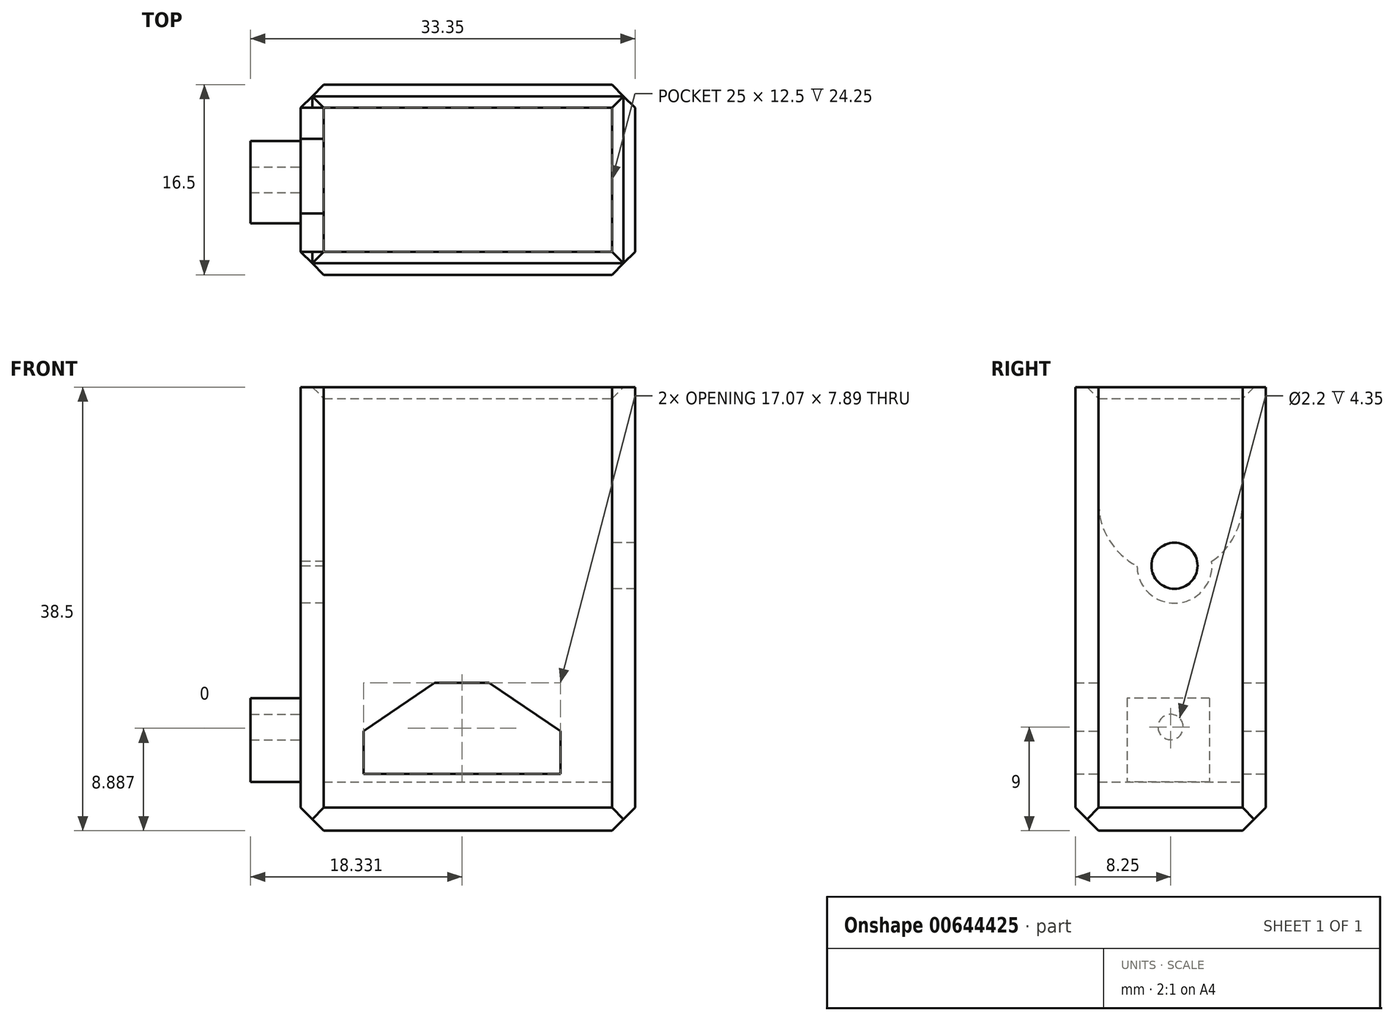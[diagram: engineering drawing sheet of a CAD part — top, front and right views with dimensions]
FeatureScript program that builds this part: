
annotation { "Feature Type Name" : "Feature", "Feature Type Description" : "" }
export const myFeature = defineFeature(function(context is Context, id is Id, definition is map)
    precondition{}
    {
        {
            var Q0;
            Q0=qCreatedBy(makeId("Top.planeOp"),FACE);
            var sketch = newSketch(context, id + "F0", { "sketchPlane" : qUnion([Q0])});
            skLineSegment(sketch, "E0.bottom", {"start": v(0, 0) * mm, "end": v(29, 0) * mm});
            skLineSegment(sketch, "E0.top", {"start": v(0, 16.5) * mm, "end": v(29, 16.5) * mm});
            skLineSegment(sketch, "E0.left", {"start": v(0, 0) * mm, "end": v(0, 16.5) * mm});
            skLineSegment(sketch, "E0.right", {"start": v(29, 0) * mm, "end": v(29, 16.5) * mm});
            skSolve(sketch);
        }
        {
            var Q0;
            Q0=makeQuery(id+"F0.imprint","IMPRINT",FACE,{"disambiguationData":[TD([[makeQuery(id+"F0.imprint","IMPRINT",EDGE,{"derivedFrom":sQuery(id+"F0.wireOp",EDGE,"E0.bottom")}),1.0]])]});
            extrude(context, id + "F1", {"entities" : qUnion([Q0]), "depth" : 38.5 * mm, "offsetDistance" : 25 * mm});
        }
        {
            var Q0;
            Q0=makeQuery(id+"F1.opExtrude","CAP_FACE",FACE,{"disambiguationData":[OSD([sQuery(id+"F0.wireOp",EDGE,"E0.bottom"),sQuery(id+"F0.wireOp",EDGE,"E0.top"),sQuery(id+"F0.wireOp",EDGE,"E0.left"),sQuery(id+"F0.wireOp",EDGE,"E0.right")])],"isStart":false});
            shell(context, id + "F2", {"entities" : qUnion([Q0]), "thickness" : 2 * mm});
        }
        {
            var Q0;
            Q0=makeQuery(id+"F2.opShell","OFFSET_FACE",FACE,{"disambiguationData":[OSD([sQuery(id+"F0.wireOp",EDGE,"E0.bottom"),sQuery(id+"F0.wireOp",EDGE,"E0.top"),sQuery(id+"F0.wireOp",EDGE,"E0.left"),sQuery(id+"F0.wireOp",EDGE,"E0.right")])]});
            extrude(context, id + "F3", {"entities" : qUnion([Q0]), "operationType" : NewBodyOperationType.ADD, "depth" : 2.25 * mm, "offsetDistance" : 25 * mm});
        }
        {
            var Q0;
            Q0=makeQuery(id+"F1.opExtrude","SWEPT_EDGE",EDGE,{"disambiguationData":[OSD([sQuery(id+"F0.wireOp",EDGE,"E0.bottom"),sQuery(id+"F0.wireOp",EDGE,"E0.left")])]});
            chamfer(context, id + "F4", {"entities" : qUnion([Q0]), "width" : 2 * mm, "tangentPropagation" : true});
        }
        {
            var Q0;
            Q0=makeQuery(id+"F1.opExtrude","SWEPT_EDGE",EDGE,{"disambiguationData":[OSD([sQuery(id+"F0.wireOp",EDGE,"E0.top"),sQuery(id+"F0.wireOp",EDGE,"E0.left")])]});
            var Q1;
            Q1=makeQuery(id+"F1.opExtrude","SWEPT_EDGE",EDGE,{"disambiguationData":[OSD([sQuery(id+"F0.wireOp",EDGE,"E0.bottom"),sQuery(id+"F0.wireOp",EDGE,"E0.right")])]});
            chamfer(context, id + "F5", {"entities" : qUnion([Q0, Q1]), "width" : 2 * mm, "tangentPropagation" : true});
        }
        {
            var Q0;
            Q0=makeQuery(id+"F1.opExtrude","SWEPT_EDGE",EDGE,{"disambiguationData":[OSD([sQuery(id+"F0.wireOp",EDGE,"E0.top"),sQuery(id+"F0.wireOp",EDGE,"E0.right")])]});
            chamfer(context, id + "F6", {"entities" : qUnion([Q0]), "width" : 2 * mm, "tangentPropagation" : true});
        }
        {
            var Q0;
            Q0=makeQuery(id+"F1.opExtrude","CAP_EDGE",EDGE,{"disambiguationData":[OSD([sQuery(id+"F0.wireOp",EDGE,"E0.bottom")])],"isStart":true});
            chamfer(context, id + "F7", {"entities" : qUnion([Q0]), "width" : 2 * mm, "tangentPropagation" : true});
        }
        {
            var Q0;
            Q0=makeQuery(id+"F1.opExtrude","CAP_EDGE",EDGE,{"disambiguationData":[OSD([sQuery(id+"F0.wireOp",EDGE,"E0.top")])],"isStart":true});
            chamfer(context, id + "F8", {"entities" : qUnion([Q0]), "width" : 2 * mm, "tangentPropagation" : true});
        }
        {
            var Q0;
            {var subQ0=sQuery(id+"F0.wireOp",EDGE,"E0.top");Q0=makeQuery(id+"F2.opShell","OFFSET_EDGE",EDGE,{"disambiguationData":[OSD([subQ0]),TDD([makeQuery(id+"F1.opExtrude","CAP_EDGE",EDGE,{"disambiguationData":[OSD([subQ0])],"isStart":false})])]});}
            var Q1;
            {var subQ0=sQuery(id+"F0.wireOp",EDGE,"E0.left");Q1=makeQuery(id+"F2.opShell","OFFSET_EDGE",EDGE,{"disambiguationData":[OSD([subQ0]),TDD([makeQuery(id+"F1.opExtrude","CAP_EDGE",EDGE,{"disambiguationData":[OSD([subQ0])],"isStart":false})])]});}
            var Q2;
            {var subQ0=sQuery(id+"F0.wireOp",EDGE,"E0.bottom");Q2=makeQuery(id+"F2.opShell","OFFSET_EDGE",EDGE,{"disambiguationData":[OSD([subQ0]),TDD([makeQuery(id+"F1.opExtrude","CAP_EDGE",EDGE,{"disambiguationData":[OSD([subQ0])],"isStart":false})])]});}
            var Q3;
            {var subQ0=sQuery(id+"F0.wireOp",EDGE,"E0.right");Q3=makeQuery(id+"F2.opShell","OFFSET_EDGE",EDGE,{"disambiguationData":[OSD([subQ0]),TDD([makeQuery(id+"F1.opExtrude","CAP_EDGE",EDGE,{"disambiguationData":[OSD([subQ0])],"isStart":false})])]});}
            chamfer(context, id + "F9", {"entities" : qUnion([Q0, Q1, Q2, Q3]), "width" : 1 * mm, "tangentPropagation" : true});
        }
        {
            var Q0;
            Q0=makeQuery(id+"F1.opExtrude","SWEPT_FACE",FACE,{"disambiguationData":[OSD([sQuery(id+"F0.wireOp",EDGE,"E0.top")])]});
            var sketch = newSketch(context, id + "F10", { "sketchPlane" : qUnion([Q0])});
            skLineSegment(sketch, "E1", {"start": v(-22.52, 8.66) * mm, "end": v(-22.52, 4.94) * mm});
            skLineSegment(sketch, "E2", {"start": v(-22.52, 4.94) * mm, "end": v(-5.44, 4.94) * mm});
            skLineSegment(sketch, "E3", {"start": v(-5.44, 4.94) * mm, "end": v(-5.44, 8.66) * mm});
            skLineSegment(sketch, "E4", {"start": v(-5.44, 8.66) * mm, "end": v(-11.62, 12.83) * mm});
            skLineSegment(sketch, "E5", {"start": v(-11.62, 12.83) * mm, "end": v(-16.34, 12.83) * mm});
            skLineSegment(sketch, "E6", {"start": v(-16.34, 12.83) * mm, "end": v(-22.52, 8.66) * mm});
            skSolve(sketch);
        }
        {
            var Q0;
            Q0=makeQuery(id+"F10.imprint","IMPRINT",FACE,{"disambiguationData":[TD([[makeQuery(id+"F10.imprint","IMPRINT",EDGE,{"derivedFrom":sQuery(id+"F10.wireOp",EDGE,"E1")}),1.0]])]});
            extrude(context, id + "F11", {"entities" : qUnion([Q0]), "operationType" : NewBodyOperationType.REMOVE, "endBound" : BoundingType.THROUGH_ALL, "oppositeDirection" : true, "depth" : 25 * mm, "offsetDistance" : 25 * mm});
        }
        {
            var Q0;
            Q0=makeQuery(id+"F1.opExtrude","CAP_EDGE",EDGE,{"disambiguationData":[OSD([sQuery(id+"F0.wireOp",EDGE,"E0.left")])],"isStart":true});
            chamfer(context, id + "F12", {"entities" : qUnion([Q0]), "width" : 2 * mm});
        }
        {
            var Q0;
            Q0=makeQuery(id+"F1.opExtrude","CAP_EDGE",EDGE,{"disambiguationData":[OSD([sQuery(id+"F0.wireOp",EDGE,"E0.right")])],"isStart":true});
            chamfer(context, id + "F13", {"entities" : qUnion([Q0]), "width" : 2 * mm});
        }
        {
            var Q0;
            Q0=makeQuery(id+"F1.opExtrude","SWEPT_FACE",FACE,{"disambiguationData":[OSD([sQuery(id+"F0.wireOp",EDGE,"E0.left")])]});
            var sketch = newSketch(context, id + "F14", { "sketchPlane" : qUnion([Q0])});
            skCircle(sketch, "E7", {"center": v(-8.25, 28.5) * mm, "radius": 6.25 * mm});
            skCircle(sketch, "E8", {"center": v(-8.59, 23) * mm, "radius": 3.25 * mm});
            skLineSegment(sketch, "E9.bottom", {"start": v(-2, 28.5) * mm, "end": v(-14.5, 28.5) * mm});
            skLineSegment(sketch, "E9.top", {"start": v(-2, 40.85) * mm, "end": v(-14.5, 40.85) * mm});
            skLineSegment(sketch, "E9.left", {"start": v(-2, 28.5) * mm, "end": v(-2, 40.85) * mm});
            skLineSegment(sketch, "E9.right", {"start": v(-14.5, 28.5) * mm, "end": v(-14.5, 40.85) * mm});
            skSolve(sketch);
        }
        {
            var Q0;
            {var subQ3=sQuery(id+"F0.wireOp",EDGE,"E0.left");var subQ8=makeQuery(id+"F1.opExtrude","CAP_EDGE",EDGE,{"disambiguationData":[OSD([subQ3])],"isStart":false});Q0=makeQuery(id+"F14.imprint","IMPRINT",FACE,{"disambiguationData":[TD([[makeQuery(id+"F14.imprint","IMPRINT",EDGE,{"derivedFrom":subQ8}),1.0]])]});}
            var Q1;
            {var subQ0=sQuery(id+"F14.wireOp",EDGE,"E9.top");Q1=makeQuery(id+"F14.imprint","IMPRINT",FACE,{"disambiguationData":[TD([[makeQuery(id+"F14.imprint","IMPRINT",EDGE,{"derivedFrom":subQ0}),1.0]])]});}
            var Q2;
            {var subQ0=sQuery(id+"F14.wireOp",EDGE,"E9.bottom");Q2=makeQuery(id+"F14.imprint","IMPRINT",FACE,{"disambiguationData":[TD([[makeQuery(id+"F14.imprint","IMPRINT",EDGE,{"derivedFrom":subQ0}),-1.0]])]});}
            var Q3;
            {var subQ0=sQuery(id+"F14.wireOp",EDGE,"E8");var subQ1=sQuery(id+"F14.wireOp",EDGE,"E7");var subQ2=makeQuery(id+"F14.imprint","INTERSECT",VERTEX,{"disambiguationData":[OD(0.0)],"derivedFrom":[subQ1,subQ0]});Q3=makeQuery(id+"F14.imprint","IMPRINT",FACE,{"disambiguationData":[TD([[makeQuery(id+"F14.imprint","IMPRINT",EDGE,{"disambiguationData":[TD([[subQ2,-1.0]])],"derivedFrom":subQ1}),1.0]])]});}
            var Q4;
            {var subQ0=sQuery(id+"F14.wireOp",EDGE,"E8");var subQ1=sQuery(id+"F14.wireOp",EDGE,"E7");var subQ2=makeQuery(id+"F14.imprint","INTERSECT",VERTEX,{"disambiguationData":[OD(0.0)],"derivedFrom":[subQ1,subQ0]});Q4=makeQuery(id+"F14.imprint","IMPRINT",FACE,{"disambiguationData":[TD([[makeQuery(id+"F14.imprint","IMPRINT",EDGE,{"disambiguationData":[TD([[subQ2,-1.0]])],"derivedFrom":subQ1}),-1.0]])]});}
            var Q5;
            {var subQ0=sQuery(id+"F14.wireOp",EDGE,"E9.bottom");Q5=makeQuery(id+"F14.imprint","IMPRINT",FACE,{"disambiguationData":[TD([[makeQuery(id+"F14.imprint","IMPRINT",EDGE,{"derivedFrom":subQ0}),1.0]])]});}
            extrude(context, id + "F15", {"entities" : qUnion([Q0, Q1, Q2, Q3, Q4, Q5]), "operationType" : NewBodyOperationType.REMOVE, "endBound" : BoundingType.UP_TO_NEXT, "oppositeDirection" : true, "depth" : 25 * mm, "offsetDistance" : 25 * mm});
        }
        {
            var Q0;
            Q0=makeQuery(id+"F2.opShell","OFFSET_FACE",FACE,{"disambiguationData":[OSD([sQuery(id+"F0.wireOp",EDGE,"E0.right")])]});
            var sketch = newSketch(context, id + "F16", { "sketchPlane" : qUnion([Q0])});
            skCircle(sketch, "E10", {"center": v(-8.59, 23) * mm, "radius": 2 * mm});
            skSolve(sketch);
        }
        {
            var Q0;
            Q0=makeQuery(id+"F16.imprint","IMPRINT",FACE,{"disambiguationData":[TD([[makeQuery(id+"F16.imprint","IMPRINT",EDGE,{"derivedFrom":sQuery(id+"F16.wireOp",EDGE,"E10")}),1.0]])]});
            extrude(context, id + "F17", {"entities" : qUnion([Q0]), "operationType" : NewBodyOperationType.REMOVE, "endBound" : BoundingType.THROUGH_ALL, "oppositeDirection" : true, "depth" : 25 * mm, "offsetDistance" : 25 * mm});
        }
        {
            var Q0;
            Q0=makeQuery(id+"F1.opExtrude","SWEPT_FACE",FACE,{"disambiguationData":[OSD([sQuery(id+"F0.wireOp",EDGE,"E0.left")])]});
            var sketch = newSketch(context, id + "F18", { "sketchPlane" : qUnion([Q0])});
            skLineSegment(sketch, "E11.bottom", {"start": v(-11.62, 11.5) * mm, "end": v(-4.48, 11.5) * mm});
            skLineSegment(sketch, "E11.top", {"start": v(-11.62, 4.25) * mm, "end": v(-4.48, 4.25) * mm});
            skLineSegment(sketch, "E11.left", {"start": v(-11.62, 11.5) * mm, "end": v(-11.62, 4.25) * mm});
            skLineSegment(sketch, "E11.right", {"start": v(-4.48, 11.5) * mm, "end": v(-4.48, 4.25) * mm});
            skCircle(sketch, "E12", {"center": v(-8.25, 9) * mm, "radius": 1.1 * mm});
            skSolve(sketch);
        }
        {
            var Q0;
            Q0=makeQuery(id+"F18.imprint","IMPRINT",FACE,{"disambiguationData":[TD([[makeQuery(id+"F18.imprint","IMPRINT",EDGE,{"derivedFrom":sQuery(id+"F18.wireOp",EDGE,"E11.bottom")}),-1.0]])]});
            extrude(context, id + "F19", {"entities" : qUnion([Q0]), "operationType" : NewBodyOperationType.ADD, "depth" : 4.35 * mm, "offsetDistance" : 25 * mm});
        }
    });
